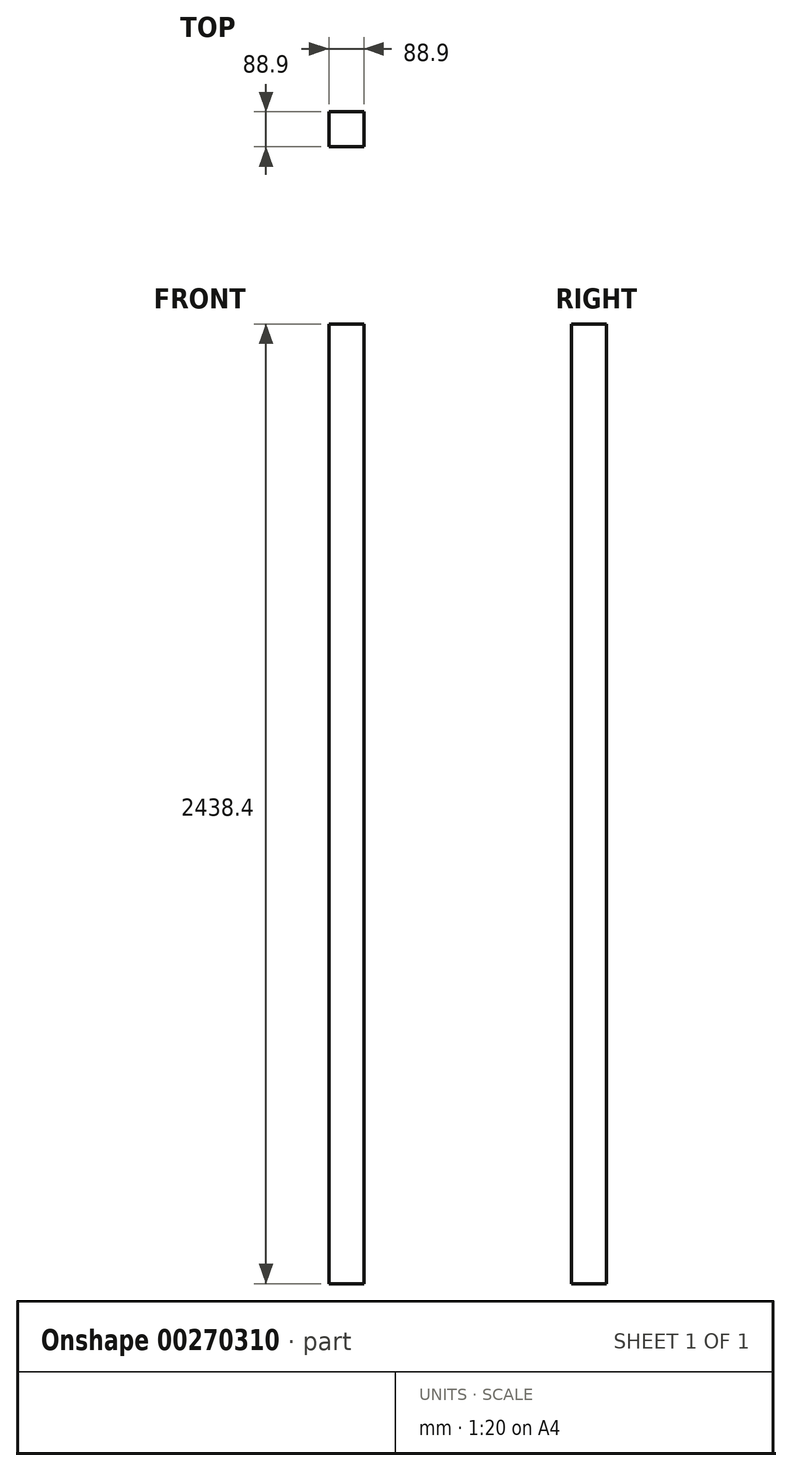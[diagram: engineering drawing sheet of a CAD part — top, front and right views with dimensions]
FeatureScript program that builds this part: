
annotation { "Feature Type Name" : "Feature", "Feature Type Description" : "" }
export const myFeature = defineFeature(function(context is Context, id is Id, definition is map)
    precondition{}
    {
        {
            var Q0;
            Q0=qCreatedBy(makeId("Top.planeOp"),FACE);
            var sketch = newSketch(context, id + "F0", { "sketchPlane" : qUnion([Q0])});
            skLineSegment(sketch, "E0.bottom", {"start": v(44.45, -44.45) * mm, "end": v(-44.45, -44.45) * mm});
            skLineSegment(sketch, "E0.top", {"start": v(44.45, 44.45) * mm, "end": v(-44.45, 44.45) * mm});
            skLineSegment(sketch, "E0.left", {"start": v(44.45, -44.45) * mm, "end": v(44.45, 44.45) * mm});
            skLineSegment(sketch, "E0.right", {"start": v(-44.45, -44.45) * mm, "end": v(-44.45, 44.45) * mm});
            skPoint(sketch, "E0.middle", {"position": v(0, 0) * mm});
            skSolve(sketch);
        }
        {
            var Q0;
            Q0=makeQuery(id+"F0.imprint","IMPRINT",FACE,{"disambiguationData":[TD([[makeQuery(id+"F0.imprint","IMPRINT",EDGE,{"derivedFrom":sQuery(id+"F0.wireOp",EDGE,"E0.bottom")}),-1.0]])]});
            extrude(context, id + "F1", {"entities" : qUnion([Q0]), "endBound" : BoundingType.SYMMETRIC, "depth" : 2438.4 * mm});
        }
    });
